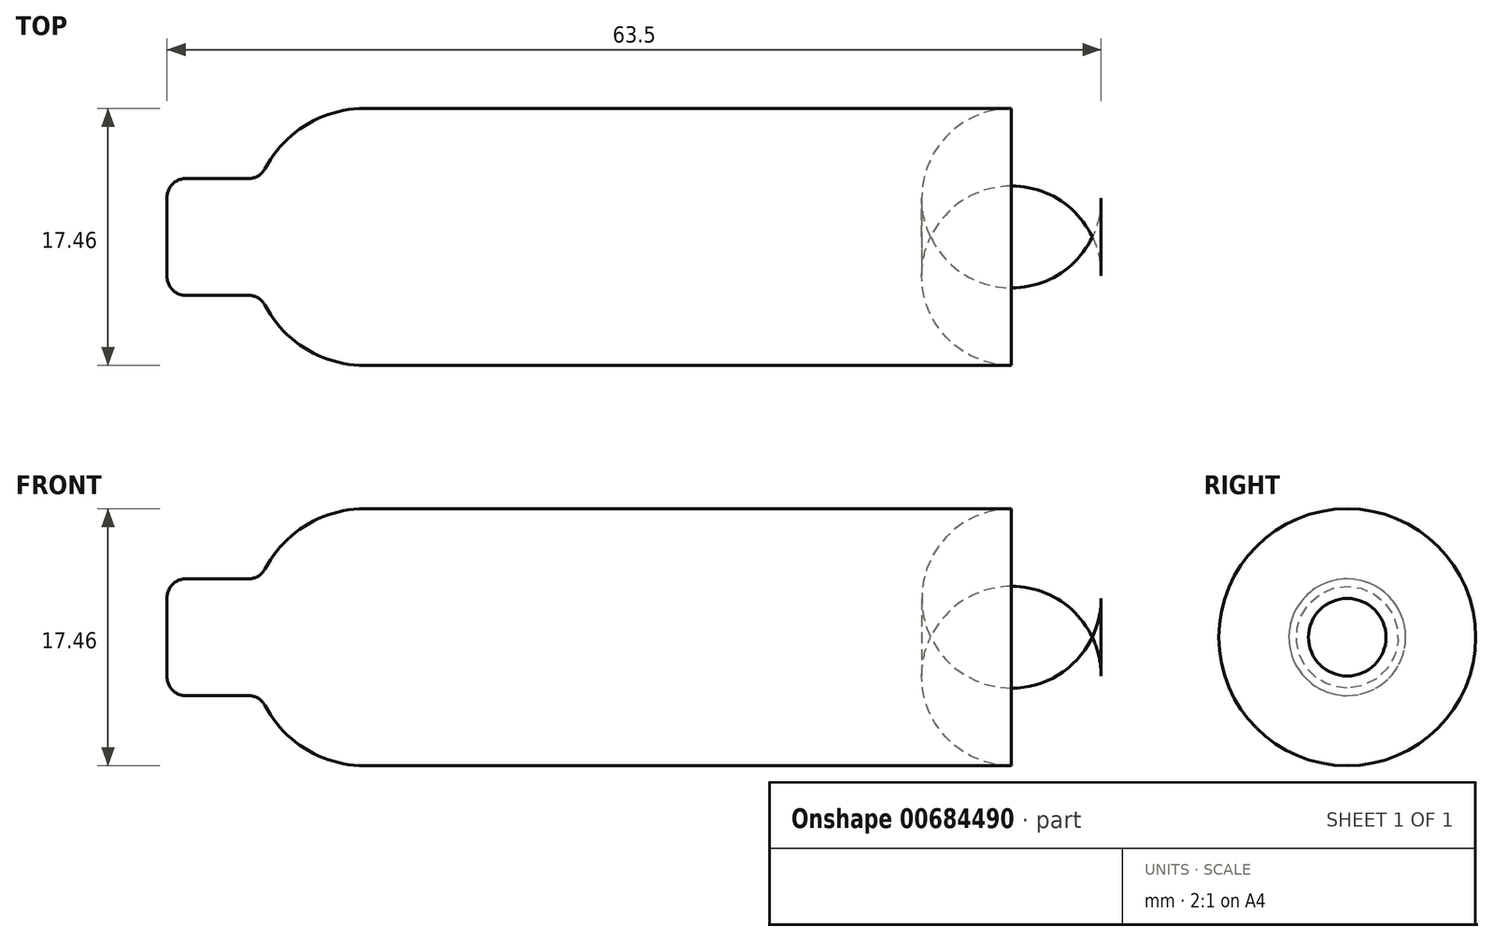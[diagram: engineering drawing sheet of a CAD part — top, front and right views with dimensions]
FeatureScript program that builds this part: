
annotation { "Feature Type Name" : "Feature", "Feature Type Description" : "" }
export const myFeature = defineFeature(function(context is Context, id is Id, definition is map)
    precondition{}
    {
        {
            var Q0;
            Q0=qCreatedBy(makeId("Front.planeOp"),FACE);
            var sketch = newSketch(context, id + "F0", { "sketchPlane" : qUnion([Q0])});
            skLineSegment(sketch, "E0", {"start": v(-25.7, 0) * mm, "end": v(37.8, 0) * mm});
            skLineSegment(sketch, "E1", {"start": v(37.8, 0) * mm, "end": v(37.8, 8.73) * mm});
            skLineSegment(sketch, "E2", {"start": v(37.8, 8.73) * mm, "end": v(-19.35, 8.73) * mm});
            skLineSegment(sketch, "E3", {"start": v(-19.35, 8.73) * mm, "end": v(-19.35, 3.97) * mm});
            skLineSegment(sketch, "E4", {"start": v(-19.35, 3.97) * mm, "end": v(-25.7, 3.97) * mm});
            skLineSegment(sketch, "E5", {"start": v(-25.7, 3.97) * mm, "end": v(-25.7, 0) * mm});
            skSolve(sketch);
        }
        {
            var Q0;
            Q0=makeQuery(id+"F0.imprint","IMPRINT",FACE,{"disambiguationData":[TD([[makeQuery(id+"F0.imprint","IMPRINT",EDGE,{"derivedFrom":sQuery(id+"F0.wireOp",EDGE,"E0")}),1.0]])]});
            var Q1;
            Q1=sQuery(id+"F0.wireOp",EDGE,"E0");
            revolve(context, id + "F1", {"entities" : qUnion([Q0]), "axis" : qUnion([Q1]), "revolveType" : RevolveType.FULL});
        }
        {
            var Q0;
            Q0=makeQuery(id+"F1.opRevolve","SWEPT_EDGE",EDGE,{"disambiguationData":[OSD([sQuery(id+"F0.wireOp",EDGE,"E1"),sQuery(id+"F0.wireOp",EDGE,"E2")])]});
            fillet(context, id + "F2", {"entities" : qUnion([Q0]), "radius" : 6.1 * mm, "tangentPropagation" : true, "allowEdgeOverflow" : false});
        }
        {
            var Q0;
            Q0=makeQuery(id+"F1.opRevolve","SWEPT_EDGE",EDGE,{"disambiguationData":[OSD([sQuery(id+"F0.wireOp",EDGE,"E2"),sQuery(id+"F0.wireOp",EDGE,"E3")])]});
            fillet(context, id + "F3", {"entities" : qUnion([Q0]), "radius" : 7.62 * mm, "tangentPropagation" : true, "allowEdgeOverflow" : false});
        }
        {
            var Q0;
            Q0=makeQuery(id+"F1.opRevolve","SWEPT_FACE",FACE,{"disambiguationData":[OSD([sQuery(id+"F0.wireOp",EDGE,"E4")])]});
            fillet(context, id + "F4", {"entities" : qUnion([Q0]), "radius" : 1.27 * mm, "tangentPropagation" : true, "allowEdgeOverflow" : false});
        }
    });
